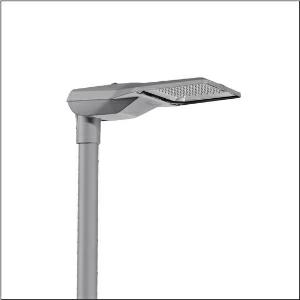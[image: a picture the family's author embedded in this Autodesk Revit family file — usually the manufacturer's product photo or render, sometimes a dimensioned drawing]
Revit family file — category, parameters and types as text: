
# Revit family: streetlight_sl_21_iq_midi___st1_0ab_5xe3m31v08nb_f534
name_source: partatom
category: Lighting Fixtures
units: mm (PartAtom-declared; Revit-internal decimal feet)

## family parameters
Cut with Voids When Loaded = No
Host = Face
Light Source = No
Part Type = Normal
Room Calculation Point = No
Round Connector Dimension = Use Diameter
Shared = No

## types (1)
- --- (1 x LED, 18970 lm, 136.6 W, 3000K)
    Apparent Load = 137 VA
    CIE Flux Codes = 40 74 97 100 100
    Color Rendering = 70
    Color Temperature = 3000K
    Default Elevation = 1800 mm
    Description = Streetlight SL 21 iQ midi, mast luminaire, primary light control with lens, of PMMA, primary optical cover: cover, of toughened safety glass, transparent, light distribution: ST1.0aB, light emission: direct distribution, primary light characteristic: asymmetric, installation type: post-top, side-entry, LED, High Power LED, rated luminous flux: 18.970lm, luminous efficacy: 139lm/W, light colour: 730, colour temperature: 3000K, control: presetting dimming logarithmic, Street-Remote, Auto-Match, Temp-Guard, Lumen-Switch, Night-Set, Smart-Wire, Light-Fading, Desk-Remote (wireless, voltage-free reading and setting of iQ features in the workshop via application-optimized NFC function/RFID function), optimised constant luminous flux control (CLO 2.0), mains connection: 230..240V, AC, 50/60Hz, start of lifetime: 137W, end of service life: 144W, reduction: 61W, luminaire housing, of diecast aluminium, powder-coated, Siteco® metallic grey (DB 702S), corrosivity category C5 mid according to DIN EN ISO 12944, please order mast flange separately, inclination adjustable: 0°, 5°, 10°, 15°, sealing non-destructively replaceable, multi-level sealing system, length: 644mm, width: 335mm, height: 110mm, mast flange for spigot size: 42mm (side-entry): 5XC10008XM4, 60/48mm (side-entry/post-top): 5XC10108XM2, 76/60mm (side-entry/post-top): 5XC10108XM1, Smart Interface above, protection rating (complete): IP66, insulation class (complete): insulation class II (safety insulation), certification: CE, ENEC, ENEC+, VDE, impact resistance: IK09, permissible operating ambient temperature for outdoor applications: -40..+50°C, standard-compliant lighting for roads and squares, packaging unit: 1 piece

Light Distribution: ST1.0aB
    Height = 111 mm
    Lamp = 1 x LED
    Lamp Light Flux = 18970 lm
    Lamp Power = 136.6 W
    Lamp count = 1
    Length = 644 mm
    Luminous efficacy = 139 lm/W
    Manufacturer = Siteco
    ModVariant = No
    Model = 5XE3M31V08NB
    Number of Poles = 1
    OnlyDefault = Yes
    Power Factor = 1
    Product Name = Streetlight SL 21 iQ midi | ST1.0aB
    Product group = mast luminaire | pylon top
    ProductGroupID = 6100
    Protection Class = Protection class II
    Protection Degree = IP 66
    RLX_Detail_Level = 1
    RLX_Emergency_Light_Flux = 0 lm
    RLX_Emergency_Type = 0
    RLX_Emergency_Type_DB = No
    RlxData = <blob elided: 91053 chars, md5=722579d5>
    Socket = socket
    Standby Power = 0 W
    System Light Flux = 18970 lm
    System Power = 137 W
    Type Comments = factory setting: luminous flux: 100 % | dim-lin: 254 | 733 mA
    Type Image = l_1004302.jpg
    URL = http://relux.com
    VarID = @adj_042179
    Voltage = 0 V
    Weight = 0.00 kg
    Width = 336 mm

## geometry (parser evidence)
native form markers: Blend x4, Sweep x12
no freeform markers — native parametric forms only
